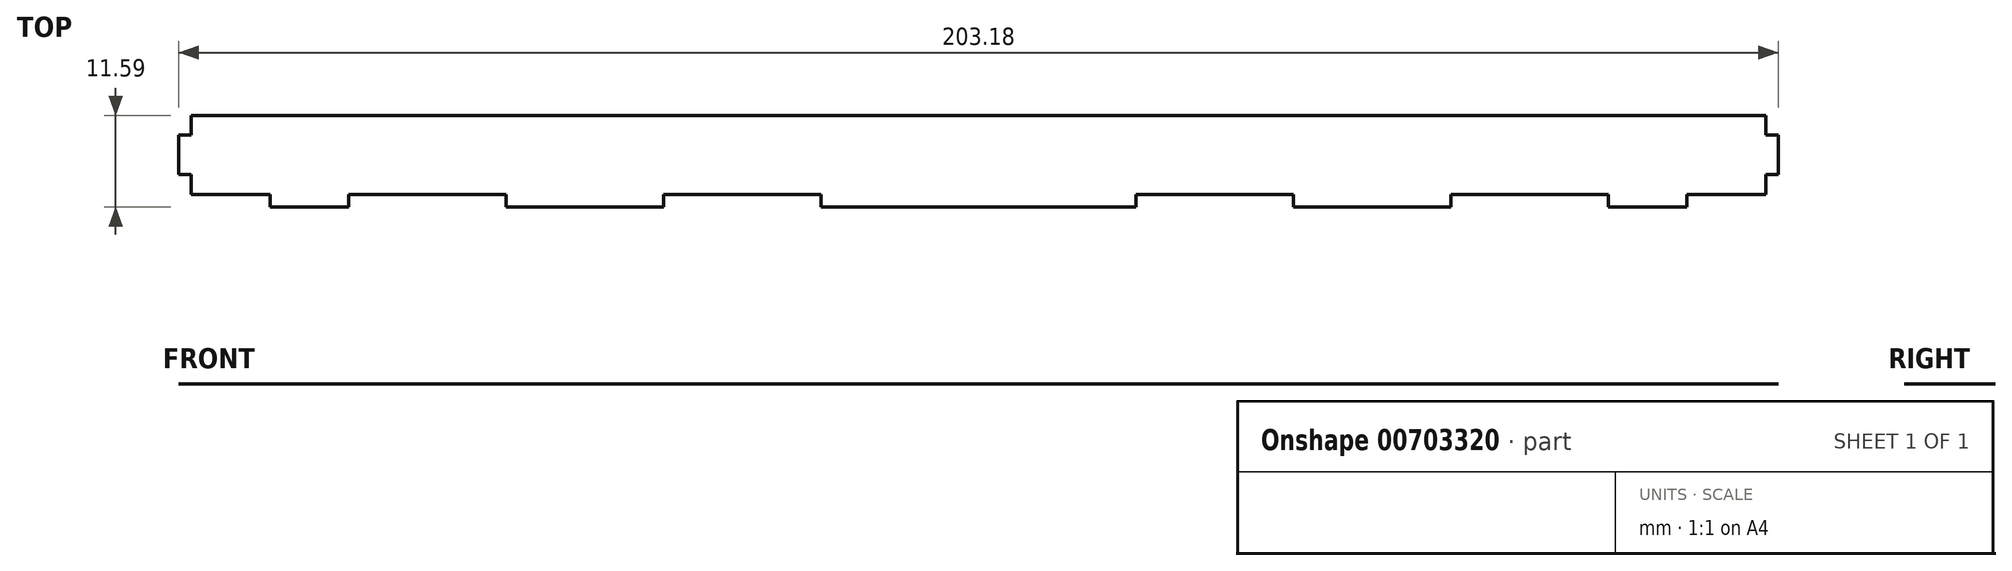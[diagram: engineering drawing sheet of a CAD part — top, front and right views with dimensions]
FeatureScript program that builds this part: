
annotation { "Feature Type Name" : "Feature", "Feature Type Description" : "" }
export const myFeature = defineFeature(function(context is Context, id is Id, definition is map)
    precondition{}
    {
        {
            var Q0;
            Q0=qCreatedBy(makeId("Top.planeOp"),FACE);
            var sketch = newSketch(context, id + "F0", { "sketchPlane" : qUnion([Q0])});
            skLineSegment(sketch, "E0.bottom", {"start": v(-100, -5) * mm, "end": v(100, -5) * mm});
            skLineSegment(sketch, "E0.top", {"start": v(-100, 5) * mm, "end": v(100, 5) * mm});
            skLineSegment(sketch, "E0.left", {"start": v(-100, -5) * mm, "end": v(-100, 5) * mm});
            skLineSegment(sketch, "E0.right", {"start": v(100, -5) * mm, "end": v(100, 5) * mm});
            skPoint(sketch, "E0.middle", {"position": v(0, 0) * mm});
            skLineSegment(sketch, "E1", {"start": v(100, 2.5) * mm, "end": v(101.59, 2.5) * mm});
            skLineSegment(sketch, "E2", {"start": v(101.59, 2.5) * mm, "end": v(101.59, -2.5) * mm});
            skLineSegment(sketch, "E3", {"start": v(101.59, -2.5) * mm, "end": v(100, -2.5) * mm});
            skLineSegment(sketch, "E4", {"start": v(-100, 2.5) * mm, "end": v(-101.59, 2.5) * mm});
            skLineSegment(sketch, "E5", {"start": v(-101.59, 2.5) * mm, "end": v(-101.59, -2.5) * mm});
            skLineSegment(sketch, "E6", {"start": v(-101.59, -2.5) * mm, "end": v(-100, -2.5) * mm});
            skLineSegment(sketch, "E7", {"start": v(-90, -5) * mm, "end": v(-90, -6.59) * mm});
            skLineSegment(sketch, "E8", {"start": v(-90, -6.59) * mm, "end": v(-80, -6.59) * mm});
            skLineSegment(sketch, "E9", {"start": v(-80, -6.59) * mm, "end": v(-80, -5) * mm});
            skLineSegment(sketch, "E10", {"start": v(-60, -5) * mm, "end": v(-60, -6.59) * mm});
            skLineSegment(sketch, "E11", {"start": v(-60, -6.59) * mm, "end": v(-40, -6.59) * mm});
            skLineSegment(sketch, "E12", {"start": v(-40, -6.59) * mm, "end": v(-40, -5) * mm});
            skLineSegment(sketch, "E13", {"start": v(40, -5) * mm, "end": v(40, -6.59) * mm});
            skLineSegment(sketch, "E14", {"start": v(40, -6.59) * mm, "end": v(60, -6.59) * mm});
            skLineSegment(sketch, "E15", {"start": v(60, -6.59) * mm, "end": v(60, -5) * mm});
            skLineSegment(sketch, "E16", {"start": v(80, -5) * mm, "end": v(80, -6.59) * mm});
            skLineSegment(sketch, "E17", {"start": v(80, -6.59) * mm, "end": v(90, -6.59) * mm});
            skLineSegment(sketch, "E18", {"start": v(90, -6.59) * mm, "end": v(90, -5) * mm});
            skLineSegment(sketch, "E19", {"start": v(-20, -5) * mm, "end": v(-20, -6.59) * mm});
            skLineSegment(sketch, "E20", {"start": v(-20, -6.59) * mm, "end": v(20, -6.59) * mm});
            skLineSegment(sketch, "E21", {"start": v(20, -6.59) * mm, "end": v(20, -5) * mm});
            skSolve(sketch);
        }
        {
            var Q0;
            Q0 = qSketchRegion(id + "F0", true);
            extrude(context, id + "F1", {"entities" : qUnion([Q0]), "depth" : 1 / 406.4 * mm, "offsetDistance" : 25 * mm});
        }
    });
